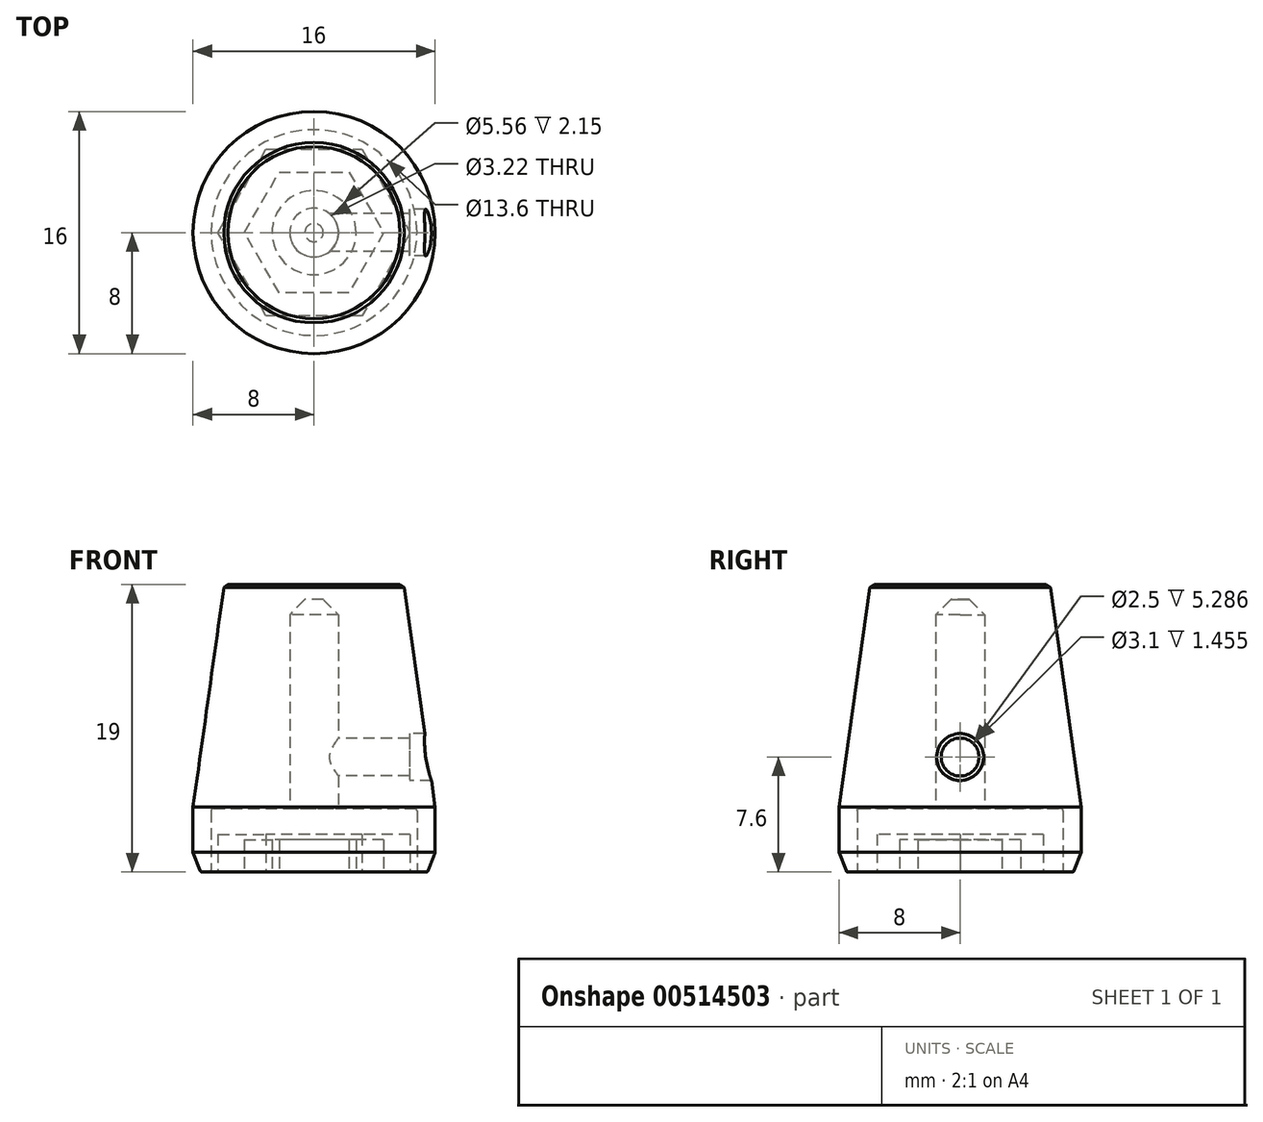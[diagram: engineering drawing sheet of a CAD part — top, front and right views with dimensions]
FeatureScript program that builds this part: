
annotation { "Feature Type Name" : "Feature", "Feature Type Description" : "" }
export const myFeature = defineFeature(function(context is Context, id is Id, definition is map)
    precondition{}
    {
        {
            assignVariable(context, id + "F0", {"name" : "majorOD", "anyValue" : 16});
        }
        {
            var Q0;
            Q0=qCreatedBy(makeId("Front.planeOp"),FACE);
            var sketch = newSketch(context, id + "F1", { "sketchPlane" : qUnion([Q0])});
            skLineSegment(sketch, "E0.bottom", {"start": v(6.8, 0) * mm, "end": v(7.5, 0) * mm});
            skLineSegment(sketch, "E0.top", {"start": v(0, 19) * mm, "end": v(5.93, 19) * mm});
            skLineSegment(sketch, "E0.left", {"start": v(0, 4.2) * mm, "end": v(0, 19) * mm, "construction": true});
            skLineSegment(sketch, "E0.right", {"start": v(8, 1.3) * mm, "end": v(8, 4.3) * mm});
            skLineSegment(sketch, "E1", {"start": v(1.6, 4.2) * mm, "end": v(6.8, 4.2) * mm});
            skLineSegment(sketch, "E2", {"start": v(6.8, 4.2) * mm, "end": v(6.8, 0) * mm});
            skLineSegment(sketch, "E3", {"start": v(1.6, 4.2) * mm, "end": v(1.6, 18) * mm});
            skLineSegment(sketch, "E4", {"start": v(1.6, 18) * mm, "end": v(0, 18) * mm});
            skLineSegment(sketch, "E5", {"start": v(0, 19) * mm, "end": v(0, 18) * mm});
            skPoint(sketch, "E6", {"position": v(0, 7.6) * mm});
            skLineSegment(sketch, "E7", {"start": v(5.93, 19) * mm, "end": v(8, 4.3) * mm});
            skLineSegment(sketch, "E8", {"start": v(8, 4.3) * mm, "end": v(8, 20.36) * mm, "construction": true});
            skPoint(sketch, "E9", {"position": v(0, 0) * mm});
            skLineSegment(sketch, "E10", {"start": v(0, 7.6) * mm, "end": v(8, 7.6) * mm, "construction": true});
            skPoint(sketch, "E11", {"position": v(8, 7.6) * mm});
            skLineSegment(sketch, "E12", {"start": v(8, 1.3) * mm, "end": v(7.5, 0) * mm});
            skSolve(sketch);
        }
        {
            var Q0;
            Q0=qSketchRegion(id+"F1",true);
            var Q1;
            Q1=sQuery(id+"F1.wireOp",EDGE,"E0.left");
            revolve(context, id + "F2", {"entities" : qUnion([Q0]), "axis" : qUnion([Q1]), "revolveType" : RevolveType.FULL});
        }
        {
            var Q0;
            Q0=makeQuery(id+"F2.opRevolve","SWEPT_EDGE",EDGE,{"disambiguationData":[OSD([sQuery(id+"F1.wireOp",EDGE,"E3"),sQuery(id+"F1.wireOp",EDGE,"E4")])]});
            chamfer(context, id + "F3", {"entities" : qUnion([Q0]), "width" : 1 * mm, "tangentPropagation" : true});
        }
        {
            var Q0;
            Q0=makeQuery(id+"F2.opRevolve","SWEPT_EDGE",EDGE,{"disambiguationData":[OSD([sQuery(id+"F1.wireOp",EDGE,"E0.top"),sQuery(id+"F1.wireOp",EDGE,"E7")])]});
            chamfer(context, id + "F4", {"entities" : qUnion([Q0]), "chamferType" : ChamferType.TWO_OFFSETS, "width1" : .25 * mm, "oppositeDirection" : false, "width2" : .2 * mm, "tangentPropagation" : true});
        }
        {
            var Q0;
            Q0=makeQuery(id+"F2.opRevolve","SWEPT_FACE",FACE,{"disambiguationData":[OSD([sQuery(id+"F1.wireOp",EDGE,"E0.bottom")])]});
            var Q1;
            Q1=makeQuery(id+"F2.opRevolve","SWEPT_EDGE",EDGE,{"disambiguationData":[OSD([sQuery(id+"F1.wireOp",EDGE,"E1"),sQuery(id+"F1.wireOp",EDGE,"E2")])]});
            var Q2;
            Q2=makeQuery(id+"F2.opRevolve","SWEPT_EDGE",EDGE,{"disambiguationData":[OSD([sQuery(id+"F1.wireOp",EDGE,"E1"),sQuery(id+"F1.wireOp",EDGE,"E3")])]});
            var Q3;
            Q3=makeQuery(id+"FZYC6JOD7CXebZJ_1.opChamfer","BLEND_EDGE",EDGE,{"blendedFrom":[makeQuery(id+"F2.opRevolve","SWEPT_EDGE",EDGE,{"disambiguationData":[OSD([sQuery(id+"F1.wireOp",EDGE,"E0.right"),sQuery(id+"F1.wireOp",EDGE,"vCOGe3Q2-wI1u-JRl4-NgCf-ssfP025QzTOs")])]}),makeQuery(id+"F2.opRevolve","SWEPT_FACE",FACE,{"disambiguationData":[OSD([sQuery(id+"F1.wireOp",EDGE,"BSaUtDve-KYLm-bPJ0-ROIl-rT6jKh3f8Nbx")])]})],"blendedInto":[makeQuery(id+"F2.opRevolve","SWEPT_FACE",FACE,{"disambiguationData":[OSD([sQuery(id+"F1.wireOp",EDGE,"BSaUtDve-KYLm-bPJ0-ROIl-rT6jKh3f8Nbx")])]})]});
            fillet(context, id + "F5", {"entities" : qUnion([Q0, Q1, Q2, Q3]), "radius" : 0.15 * mm, "tangentPropagation" : true, "allowEdgeOverflow" : false});
        }
        {
            var Q0;
            Q0=sQuery(id+"F1.wireOp",EDGE,"E0.right");
            cPlane(context, id + "F6", {"entities" : qUnion([Q0]), "cplaneType" : CPlaneType.LINE_ANGLE, "offset" : 25 * mm, "angle" : 0 * degree, "width" : 150 * mm, "height" : 150 * mm});
        }
        {
            var Q0;
            Q0=qCreatedBy(id+"F6.planeOp",FACE);
            var sketch = newSketch(context, id + "F7", { "sketchPlane" : qUnion([Q0])});
            skPoint(sketch, "E13.0", {"position": v(0, 7.6) * mm});
            skSolve(sketch);
        }
        {
            var Q0;
            Q0=sQuery(id+"F7.wireOp",VERTEX,"E13.0");
            var Q1;
            Q1=makeQuery(id+"F2.opRevolve","SWEPT_BODY",BODY,{"disambiguationData":[OSD([sQuery(id+"F1.wireOp",EDGE,"E0.bottom"),sQuery(id+"F1.wireOp",EDGE,"E0.top"),sQuery(id+"F1.wireOp",EDGE,"E0.right"),sQuery(id+"F1.wireOp",EDGE,"E1"),sQuery(id+"F1.wireOp",EDGE,"E2"),sQuery(id+"F1.wireOp",EDGE,"BSaUtDve-KYLm-bPJ0-ROIl-rT6jKh3f8Nbx"),sQuery(id+"F1.wireOp",EDGE,"vCOGe3Q2-wI1u-JRl4-NgCf-ssfP025QzTOs"),sQuery(id+"F1.wireOp",EDGE,"E3"),sQuery(id+"F1.wireOp",EDGE,"E4"),sQuery(id+"F1.wireOp",EDGE,"E5"),sQuery(id+"F1.wireOp",EDGE,"E7")])]});
            hole(context, id + "F8", {"style" : HoleStyle.C_BORE, "endStyle" : HoleEndStyle.BLIND, "holeDiameter" : 2.5 * mm, "cBoreDiameter" : 3.1 * mm, "cBoreDepth" : 1 * mm, "majorDiameter" : 5 * mm, "holeDepth" : (getVariable(context, 'majorOD') / 2) * mm, "isTappedThrough" : true, "tappedDepth" : 12 * mm, "tapClearance" : 3, "locations" : qUnion([Q0]), "scope" : qUnion([Q1]), "startStyle" : HoleStartStyle.PART});
        }
        {
            var Q0;
            Q0=qCreatedBy(makeId("Top.planeOp"),FACE);
            var sketch = newSketch(context, id + "F9", { "sketchPlane" : qUnion([Q0])});
            skCircle(sketch, "E14.cCircle", {"center": v(0, 0) * mm, "radius": 4 * mm, "construction": true});
            skLineSegment(sketch, "E14.0", {"start": v(2.3, -4) * mm, "end": v(-2.3, -4) * mm});
            skLineSegment(sketch, "E14.1", {"start": v(-2.3, -4) * mm, "end": v(-4.6, 0) * mm});
            skLineSegment(sketch, "E14.2", {"start": v(-4.6, 0) * mm, "end": v(-2.3, 4) * mm});
            skLineSegment(sketch, "E14.3", {"start": v(-2.3, 4) * mm, "end": v(2.3, 4) * mm});
            skLineSegment(sketch, "E14.4", {"start": v(2.3, 4) * mm, "end": v(4.6, 0) * mm});
            skLineSegment(sketch, "E14.5", {"start": v(4.6, 0) * mm, "end": v(2.3, -4) * mm});
            skPoint(sketch, "E14.0.midPoint", {"position": v(0, -4) * mm});
            skCircle(sketch, "E15", {"center": v(0, 0) * mm, "radius": 2.78 * mm});
            skSolve(sketch);
        }
        {
            var Q0;
            Q0=qSketchRegion(id+"F9",true);
            extrude(context, id + "F10", {"entities" : qUnion([Q0]), "depth" : 2.15 * mm, "offsetDistance" : 25 * mm});
        }
        {
            var Q0;
            Q0=qCreatedBy(makeId("Top.planeOp"),FACE);
            var sketch = newSketch(context, id + "F11", { "sketchPlane" : qUnion([Q0])});
            skCircle(sketch, "E16.cCircle", {"center": v(0, 0) * mm, "radius": 5.5 * mm, "construction": true});
            skLineSegment(sketch, "E16.0", {"start": v(3.18, -5.5) * mm, "end": v(-3.18, -5.5) * mm});
            skLineSegment(sketch, "E16.1", {"start": v(-3.18, -5.5) * mm, "end": v(-6.35, 0) * mm});
            skLineSegment(sketch, "E16.2", {"start": v(-6.35, 0) * mm, "end": v(-3.18, 5.5) * mm});
            skLineSegment(sketch, "E16.3", {"start": v(-3.18, 5.5) * mm, "end": v(3.18, 5.5) * mm});
            skLineSegment(sketch, "E16.4", {"start": v(3.18, 5.5) * mm, "end": v(6.35, 0) * mm});
            skLineSegment(sketch, "E16.5", {"start": v(6.35, 0) * mm, "end": v(3.18, -5.5) * mm});
            skPoint(sketch, "E16.0.midPoint", {"position": v(0, -5.5) * mm});
            skSolve(sketch);
        }
        {
            var Q0;
            Q0 = qSketchRegion(id + "F11", true);
            extrude(context, id + "F12", {"entities" : qUnion([Q0]), "depth" : 2.5 * mm, "offsetDistance" : 25 * mm});
        }
    });
